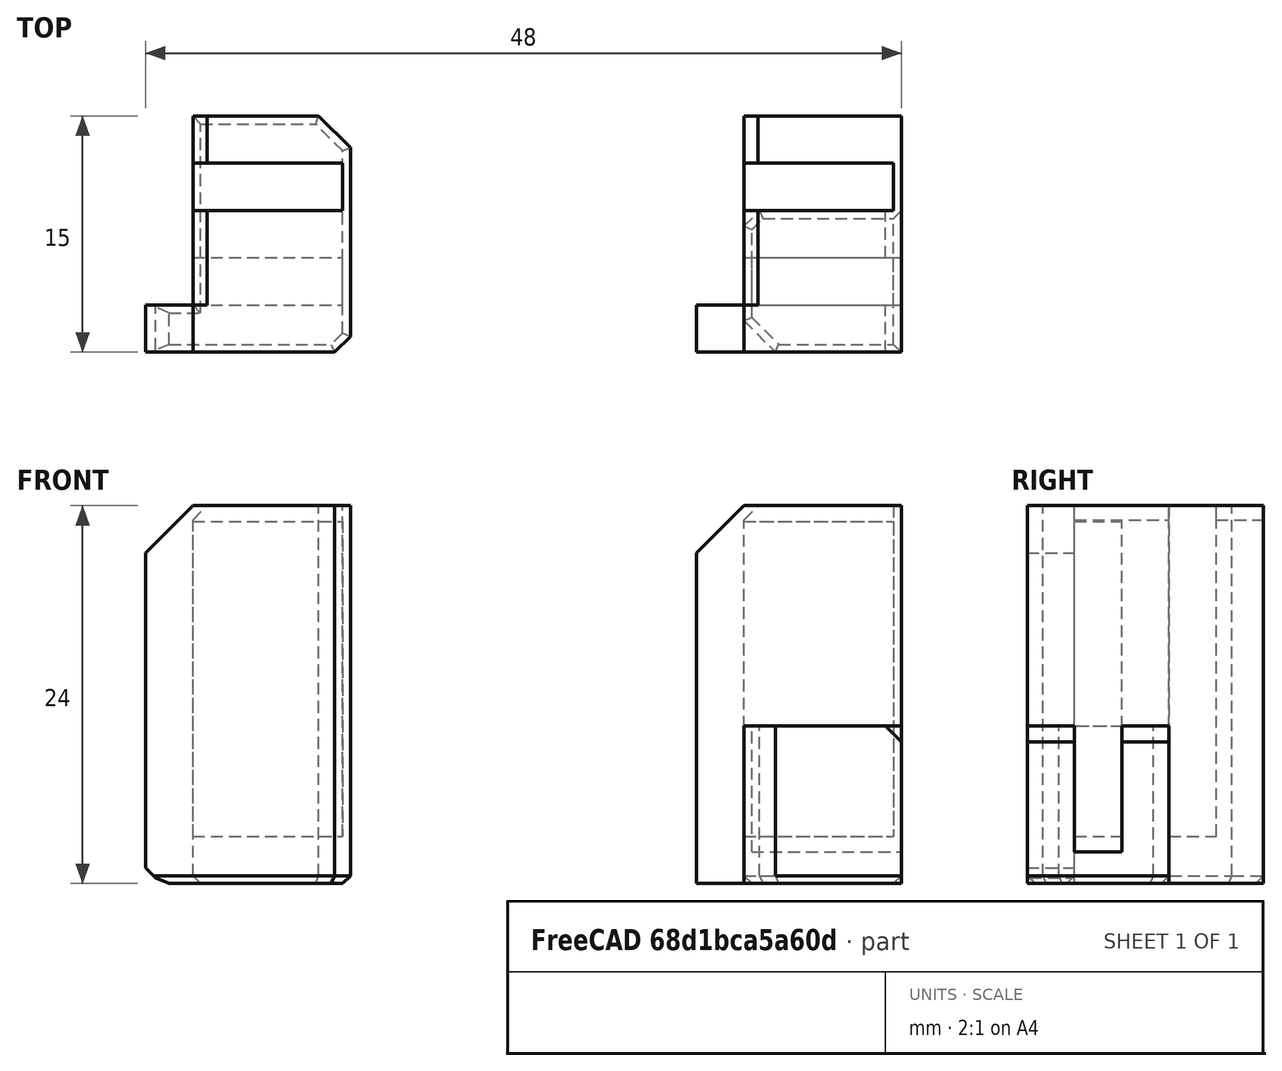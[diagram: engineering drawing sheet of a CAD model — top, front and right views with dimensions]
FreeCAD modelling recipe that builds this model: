
FCSTD DOCUMENT  (FreeCAD 0.18R14555 (Git shallow))
Label: enclosure-handle
License: All rights reserved
LicenseURL: http://en.wikipedia.org/wiki/All_rights_reserved
objects: Part::Box×10, Part::Chamfer×10, Part::MultiFuse×2, Part::Feature×2, Part::Cut×1
note: 25 computed .brp shape members not serialized (recipe doc carries the construction recipe); baked Part::Feature solids carry a one-line shape summary decoded from their .brp

FEATURE [Part::Box] Box  label="magnet"
  AttacherType = Attacher::AttachEngine3D
  Height = 20
  Length = 10
  Placement = pos=(0,-3,3) rot=(0,0,1;0rad)
  Width = 3
FEATURE [Part::Box] Box001  label="Cube"
  AttacherType = Attacher::AttachEngine3D
  Height = 24
  Length = 0.5
  Placement = pos=(9.5,-6,0) rot=(0,0,1;0rad)
  Width = 15
FEATURE [Part::Box] Box003  label="Cube002"
  AttacherType = Attacher::AttachEngine3D
  Height = 24
  Length = 10
  Placement = pos=(0,6,0) rot=(0,0,1;0rad)
  Width = 3
FEATURE [Part::Box] Box008  label="Cube006"
  AttacherType = Attacher::AttachEngine3D
  Height = 3
  Length = 10
  Placement = pos=(0,-6,0) rot=(0,0,1;0rad)
  Width = 15
FEATURE [Part::Box] Box005  label="magnet001"
  AttacherType = Attacher::AttachEngine3D
  Height = 24
  Length = 10
  Placement = pos=(0,-6,0) rot=(0,0,1;0rad)
  Width = 9
FEATURE [Part::Cut] Cut
  Base = -> Box005
  Tool = -> Box
FEATURE [Part::Box] Box009  label="Cube007"
  AttacherType = Attacher::AttachEngine3D
  Height = 24
  Length = 4
  Placement = pos=(-3,-6,0) rot=(0,0,1;0rad)
  Width = 3
FEATURE [Part::Chamfer] Chamfer
  Base = -> Box009
  Edges = 1 edges r=3: [Edge2]
FEATURE [Part::Chamfer] Chamfer001
  Base = -> Box003
  Edges = 1 edges r=0.9: [Edge2]
FEATURE [Part::Chamfer] Chamfer002
  Base = -> Cut
  Edges = 1 edges r=0.9: [Edge2]
FEATURE [Part::MultiFuse] Fusion
  Shapes = -> [Chamfer002,Box008,Chamfer,Box001,Chamfer001]
FEATURE [Part::Feature] Fusion001
  shape: bbox 13 x 15 x 24 mm, 19 faces (baked)
FEATURE [Part::Chamfer] Chamfer003
  Base = -> Fusion001
  Edges = 1 edges r=2: [Edge51]
FEATURE [Part::Chamfer] Chamfer004
  Base = -> Chamfer003
  Edges = 1 edges r=1: [Edge24]
FEATURE [Part::Chamfer] Chamfer005
  Base = -> Chamfer004
  Edges = 1 edges r=1: [Edge6]
FEATURE [Part::Chamfer] Chamfer006  label="handle"
  Base = -> Chamfer005
  Edges = 8 edges r=0.5: [Edge1,Edge2,Edge3,Edge4,Edge5,Edge6,Edge7,Edge8]
  Placement = pos=(-35,0,0) rot=(0,0,1;0rad)
FEATURE [Part::Box] Box010  label="Cube008"
  AttacherType = Attacher::AttachEngine3D
  Height = 10
  Length = 10
  Width = 3
FEATURE [Part::Box] Box011  label="Cube009"
  AttacherType = Attacher::AttachEngine3D
  Height = 10
  Length = 10
  Placement = pos=(0,-6,0) rot=(0,0,1;0rad)
  Width = 3
FEATURE [Part::Box] Box012  label="Cube010"
  AttacherType = Attacher::AttachEngine3D
  Height = 2
  Length = 10
  Placement = pos=(0,-6,0) rot=(0,0,1;0rad)
  Width = 9
FEATURE [Part::Box] Box013  label="Cube011"
  AttacherType = Attacher::AttachEngine3D
  Height = 10
  Length = 0.5
  Placement = pos=(0,-6,0) rot=(0,0,1;0rad)
  Width = 9
FEATURE [Part::MultiFuse] Fusion002
  Shapes = -> [Box013,Box010,Box011,Box012]
FEATURE [Part::Feature] Fusion002001  label="Fusion003"
  shape: bbox 10 x 9 x 10 mm, 10 faces (baked)
FEATURE [Part::Chamfer] Chamfer007
  Base = -> Fusion002001
  Edges = 1 edges r=2: [Edge1]
FEATURE [Part::Chamfer] Chamfer008
  Base = -> Chamfer007
  Edges = 3 edges r=1: [Edge3,Edge7,Edge11]
FEATURE [Part::Chamfer] Chamfer009
  Base = -> Chamfer008
  Edges = 6 edges r=0.5: [Edge4,Edge14,Edge16,Edge18,Edge19,Edge20]
